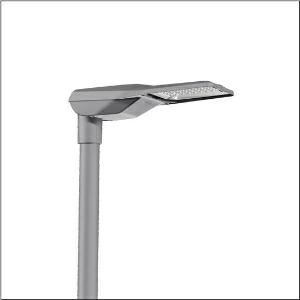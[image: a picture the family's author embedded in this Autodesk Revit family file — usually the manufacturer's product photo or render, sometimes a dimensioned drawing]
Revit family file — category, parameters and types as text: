
# Revit family: streetlight_sl_21_iq_mini___st1_5a_5xe2p31g08hb_126e
name_source: partatom
category: Lighting Fixtures
units: mm (PartAtom-declared; Revit-internal decimal feet)

## family parameters
Cut with Voids When Loaded = No
Host = Face
Light Source = No
Part Type = Normal
Room Calculation Point = No
Round Connector Dimension = Use Diameter
Shared = No

## types (1)
- --- (1 x LED, 9290 lm, 70.9 W, 3000K)
    Apparent Load = 71 VA
    CIE Flux Codes = 22 53 95 100 100
    Color Rendering = 70
    Color Temperature = 3000K
    Default Elevation = 1800 mm
    Description = Streetlight SL 21 iQ mini, mast luminaire, primary light control with lens, of PMMA, primary optical cover: cover, of toughened safety glass, transparent, light distribution: ST1.5a, light emission: direct distribution, primary light characteristic: asymmetric, installation type: post-top, side-entry, LED, High Power LED, rated luminous flux: 9.290lm, luminous efficacy: 131lm/W, light colour: 730, colour temperature: 3000K, control: Street-Remote, Auto-Match, Temp-Guard, Lumen-Switch, Night-Set, Smart-Wire, Light-Fading, Desk-Remote (wireless, voltage-free reading and setting of iQ features in the workshop via application-optimized NFC function/RFID function), optimised constant luminous flux control (CLO 2.0), presetting dimming linear, mains connection: 220..240V, AC, 50/60Hz, start of lifetime: 71W, end of service life: 75W, reduction: 31W, luminaire housing, of diecast aluminium, powder-coated, Siteco® metallic grey (DB 702S), corrosivity category C5 mid according to DIN EN ISO 12944, please order mast flange separately, inclination adjustable: 0°, 5°, 10°, 15°, sealing non-destructively replaceable, multi-level sealing system, length: 628mm, width: 235mm, height: 110mm, mast flange for spigot size: 42mm (side-entry): 5XC10008XM4, 60/48mm (side-entry/post-top): 5XC10108XM2, 76/60mm (side-entry/post-top): 5XC10108XM1, protection rating (complete): IP66, insulation class (complete): insulation class II (safety insulation), certification: CE, ENEC, ENEC+, VDE, impact resistance: IK09, permissible operating ambient temperature for outdoor applications: -40..+50°C, standard-compliant lighting for roads and squares, packaging unit: 1 piece

Light Distribution: ST1.5a
    Height = 110 mm
    Lamp = 1 x LED
    Lamp Light Flux = 9290 lm
    Lamp Power = 70.9 W
    Lamp count = 1
    Length = 625 mm
    Luminous efficacy = 131 lm/W
    Manufacturer = Siteco
    ModVariant = No
    Model = 5XE2P31G08HB
    Number of Poles = 1
    OnlyDefault = Yes
    Power Factor = 1
    Product Name = Streetlight SL 21 iQ mini | ST1.5a
    Product group = mast luminaire | pylon top
    ProductGroupID = 6100
    Protection Class = Protection class II
    Protection Degree = IP 66
    RLX_Detail_Level = 1
    RLX_Emergency_Light_Flux = 0 lm
    RLX_Emergency_Type = 0
    RLX_Emergency_Type_DB = No
    RlxData = <blob elided: 96461 chars, md5=fa129195>
    Socket = socket
    Standby Power = 0 W
    System Light Flux = 9290 lm
    System Power = 71 W
    Type Comments = factory setting: luminous flux: 100 % | dim-lin: 254 | 711 mA
    Type Image = l_1003519.jpg
    URL = http://relux.com
    VarID = @adj_089393
    Voltage = 0 V
    Weight = 0.00 kg
    Width = 234 mm

## geometry (parser evidence)
native form markers: Blend x4, Sweep x13
no freeform markers — native parametric forms only
